# Revit family: LAVK 1 WIDE
name_source: partatom
category: Mechanical Equipment
units: mm (PartAtom-declared; Revit-internal decimal feet)

## family parameters
Always vertical = Yes
Classification = None
Cut with Voids When Loaded = No
OmniClass Number = 23.75.00.00
OmniClass Title = Climate Control (HVAC)
Part Type = Normal
Room Calculation Point = No
Round Connector Dimension = Use Diameter
Shared = No
Work Plane-Based = No

## types (7) — shared parameters
Copper Pipes = Copper Pipe
Description = levitor condenser LAV (K-MTR)
Fan001 = Yes
Full Load Amps (FLA) = Amps-1
Full load Amps (FLA)-2 = Amps-2
Height of base = 10.5 "
Inlet Pipe Size = 2"
LegA1 = No
Manufacturer = HUSSMANN CORPORATION
Model = LAVK 1 WIDE
Outlet Pipe Size = 2"
Phase = 3
Revit Family Dates = 04-26-2023 HM
Steel = Steel
TEXT = 1 "
Type Comments = Systems
Voltage = 460 V
Voltage - 2 = 208 V
legA = No

## per-type parameters (varying)
| type | Controller box 5,6,7 fans | Controller box upto 4 fans | Fan002 | Fan003 | Fan004 | Fan005 | Fan006 | Fan007 | LegB | LegC | LegD | LegE | LegF | Over all height | URL | Unit Width |
| LAVK 1X1 | No | Yes | No | No | No | No | No | No | No | No | No | No | No | 54 " |  | 58 " |
| LAVK 2X1 | No | Yes | Yes | No | No | No | No | No | No | No | No | No | No | 54 " |  | 112 " |
| LAVK 3X1 | No | Yes | Yes | Yes | No | No | No | No | Yes | No | No | No | No | 54 " |  | 166 " |
| LAVK 4X1 | No | Yes | Yes | Yes | Yes | No | No | No | No | Yes | No | No | No | 54 " |  | 220 " |
| LAVK 5X1 | Yes | No | Yes | Yes | Yes | Yes | No | No | No | No | Yes | No | No | 58.5 " |  | 274 " |
| LAVK 6X1 | Yes | No | Yes | Yes | Yes | Yes | Yes | No | No | No | No | Yes | No | 58.5 " |  | 328 " |
| LAVK 7X1 | Yes | No | Yes | Yes | Yes | Yes | Yes | Yes | No | No | No | No | Yes | 58.5 " | www.krack.com | 382 " |

## geometry (parser evidence)
native form markers: Blend x8, Sweep x87
no freeform markers — native parametric forms only
